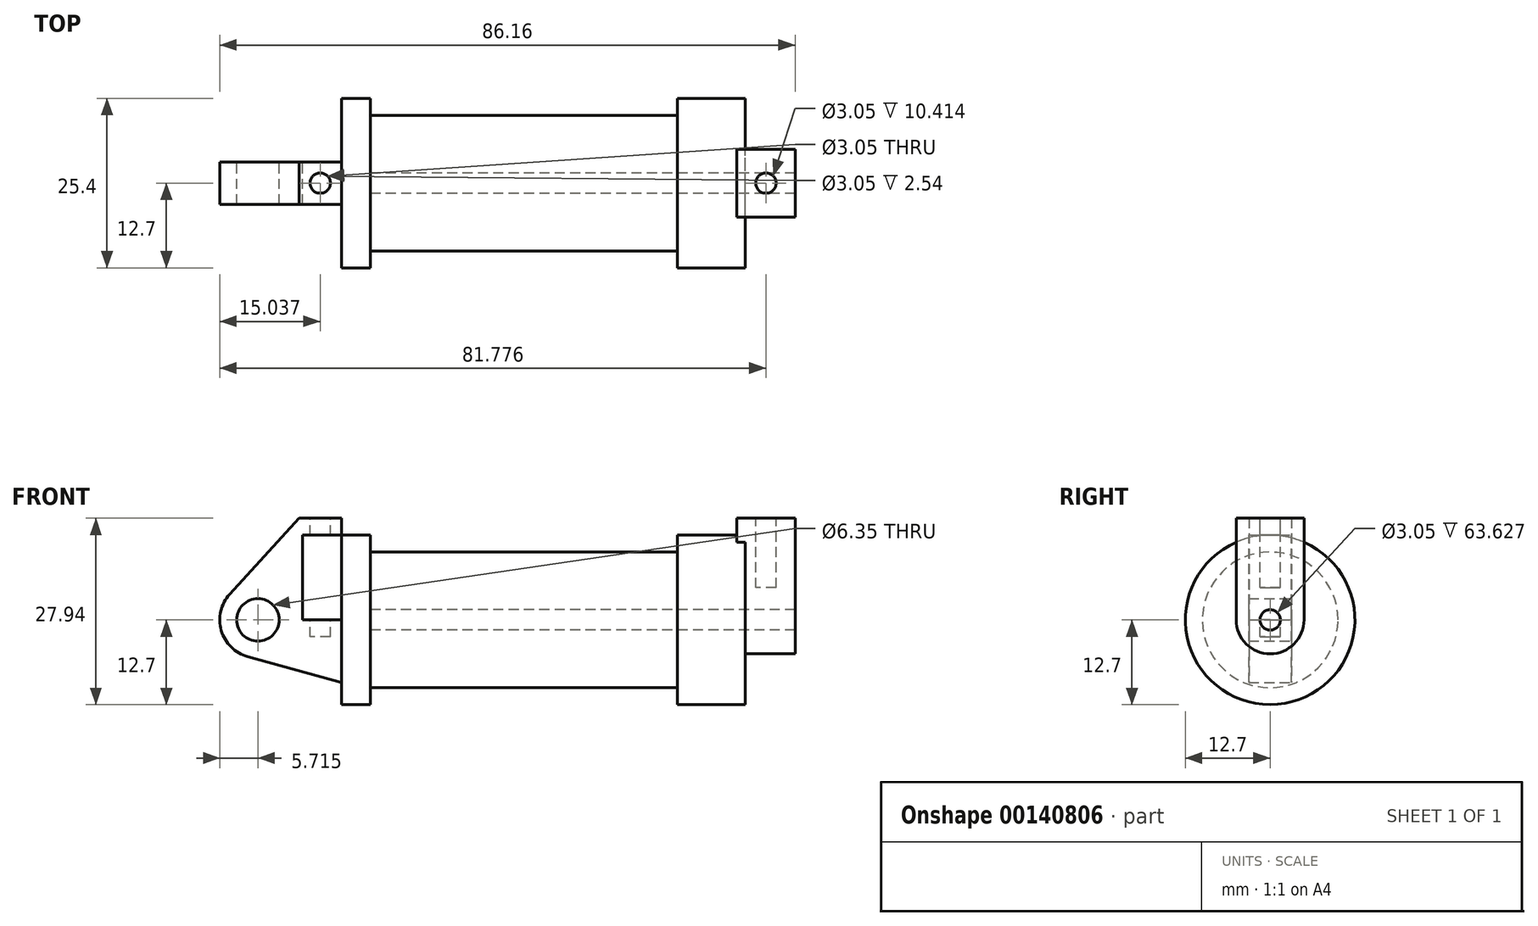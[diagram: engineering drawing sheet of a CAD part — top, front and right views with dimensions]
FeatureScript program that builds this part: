
annotation { "Feature Type Name" : "Feature", "Feature Type Description" : "" }
export const myFeature = defineFeature(function(context is Context, id is Id, definition is map)
    precondition{}
    {
        {
            var Q0;
            Q0=qCreatedBy(makeId("Front.planeOp"),FACE);
            var sketch = newSketch(context, id + "F0", { "sketchPlane" : qUnion([Q0])});
            skLineSegment(sketch, "E0", {"start": v(0, 0) * mm, "end": v(0, 12.7) * mm});
            skLineSegment(sketch, "E1", {"start": v(0, 12.7) * mm, "end": v(10.16, 12.7) * mm});
            skLineSegment(sketch, "E2", {"start": v(10.16, 12.7) * mm, "end": v(10.16, 10.16) * mm});
            skLineSegment(sketch, "E3", {"start": v(10.16, 10.16) * mm, "end": v(56.13, 10.16) * mm});
            skLineSegment(sketch, "E4", {"start": v(56.13, 10.16) * mm, "end": v(56.13, 12.7) * mm});
            skLineSegment(sketch, "E5", {"start": v(56.13, 12.7) * mm, "end": v(66.3, 12.7) * mm});
            skLineSegment(sketch, "E6", {"start": v(66.3, 12.7) * mm, "end": v(66.3, 0) * mm});
            skLineSegment(sketch, "E7", {"start": v(66.3, 0) * mm, "end": v(0, 0) * mm});
            skLineSegment(sketch, "E8", {"start": v(5.84, 15.24) * mm, "end": v(-0.5, 15.24) * mm});
            skLineSegment(sketch, "E9", {"start": v(-0.5, 15.24) * mm, "end": v(-10.88, 3.85) * mm});
            skLineSegment(sketch, "E10", {"start": v(0, 0) * mm, "end": v(-6.65, 0) * mm});
            skCircle(sketch, "E11", {"center": v(-6.65, 0) * mm, "radius": 5.72 * mm});
            skCircle(sketch, "E12", {"center": v(-6.65, 0) * mm, "radius": 3.18 * mm});
            skLineSegment(sketch, "E13", {"start": v(5.84, 15.24) * mm, "end": v(5.84, -9.4) * mm});
            skLineSegment(sketch, "E14", {"start": v(5.84, -9.4) * mm, "end": v(-8.18, -5.5) * mm});
            skSolve(sketch);
        }
        {
            var Q0;
            {var subQ3=sQuery(id+"F0.wireOp",EDGE,"E0");Q0=makeQuery(id+"F0.imprint","IMPRINT",FACE,{"disambiguationData":[TD([[makeQuery(id+"F0.imprint","IMPRINT",EDGE,{"derivedFrom":subQ3}),1.0]])]});}
            var Q1;
            {var subQ0=sQuery(id+"F0.wireOp",EDGE,"E14");Q1=makeQuery(id+"F0.imprint","IMPRINT",FACE,{"disambiguationData":[TD([[makeQuery(id+"F0.imprint","IMPRINT",EDGE,{"derivedFrom":subQ0}),-1.0]])]});}
            var Q2;
            {var subQ4=sQuery(id+"F0.wireOp",EDGE,"E12");Q2=makeQuery(id+"F0.imprint","IMPRINT",FACE,{"disambiguationData":[TD([[makeQuery(id+"F0.imprint","IMPRINT",EDGE,{"derivedFrom":subQ4}),-1.0]])]});}
            extrude(context, id + "F1", {"entities" : qUnion([Q0, Q1, Q2]), "endBound" : BoundingType.SYMMETRIC, "depth" : 6.35 * mm});
        }
        {
            var Q0;
            {var subQ0=sQuery(id+"F0.wireOp",EDGE,"E2");Q0=makeQuery(id+"F0.imprint","IMPRINT",FACE,{"disambiguationData":[TD([[makeQuery(id+"F0.imprint","IMPRINT",EDGE,{"derivedFrom":subQ0}),-1.0]])]});}
            var Q1;
            Q1=sQuery(id+"F0.wireOp",EDGE,"E7");
            revolve(context, id + "F2", {"entities" : qUnion([Q0]), "axis" : qUnion([Q1]), "revolveType" : RevolveType.FULL});
        }
        {
            var Q0;
            Q0=makeQuery(id+"F2.opRevolve","SWEPT_FACE",FACE,{"disambiguationData":[OSD([sQuery(id+"F0.wireOp",EDGE,"E6")])]});
            var sketch = newSketch(context, id + "F3", { "sketchPlane" : qUnion([Q0])});
            skCircle(sketch, "E15", {"center": v(0, 0) * mm, "radius": 1.52 * mm});
            skCircle(sketch, "E16", {"center": v(0, 0) * mm, "radius": 5.08 * mm});
            skLineSegment(sketch, "E17", {"start": v(-5.08, 0) * mm, "end": v(-5.08, 15.24) * mm});
            skLineSegment(sketch, "E18", {"start": v(5.08, 0) * mm, "end": v(5.08, 15.24) * mm});
            skLineSegment(sketch, "E19", {"start": v(5.08, 15.24) * mm, "end": v(-5.08, 15.24) * mm});
            skSolve(sketch);
        }
        {
            var Q0;
            Q0 = qSketchRegion(id + "F3", true);
            extrude(context, id + "F4", {"entities" : qUnion([Q0]), "operationType" : NewBodyOperationType.ADD, "oppositeDirection" : true, "depth" : 1.27 * mm});
        }
        {
            var Q0;
            Q0 = qSketchRegion(id + "F3", true);
            extrude(context, id + "F5", {"entities" : qUnion([Q0]), "operationType" : NewBodyOperationType.ADD, "depth" : 7.5 * mm});
        }
        {
            var Q0;
            Q0=makeQuery(id+"F3.imprint","IMPRINT",FACE,{"disambiguationData":[TD([[makeQuery(id+"F3.imprint","IMPRINT",EDGE,{"derivedFrom":sQuery(id+"F3.wireOp",EDGE,"E15")}),1.0]])]});
            var Q1;
            Q1=sQuery(id+"F3.wireOp",EDGE,"E15");
            var Q2;
            Q2=makeQuery(id+"F2.opRevolve","SWEPT_FACE",FACE,{"disambiguationData":[OSD([sQuery(id+"F0.wireOp",EDGE,"E2")])]});
            extrude(context, id + "F6", {"entities" : qUnion([Q0]), "operationType" : NewBodyOperationType.REMOVE, "surfaceEntities" : qUnion([Q1]), "endBound" : BoundingType.UP_TO_SURFACE, "oppositeDirection" : true, "endBoundEntityFace" : qUnion([Q2]), "depth" : 25.4 * mm});
        }
        {
            var Q0;
            {var subQ0=sQuery(id+"F3.wireOp",EDGE,"E19");Q0=makeQuery(id+"F5.boolean.opBoolean","MERGE",FACE,{"derivedFrom":[makeQuery(id+"F4.opExtrude","SWEPT_FACE",FACE,{"disambiguationData":[OSD([subQ0])]}),makeQuery(id+"F5.opExtrude","SWEPT_FACE",FACE,{"disambiguationData":[OSD([subQ0])]})]});}
            var sketch = newSketch(context, id + "F7", { "sketchPlane" : qUnion([Q0])});
            skCircle(sketch, "E20", {"center": v(69.4, 0) * mm, "radius": 1.52 * mm});
            skPoint(sketch, "E20.centerSnap0", {"position": v(69.4, 5.08) * mm});
            skPoint(sketch, "E20.centerSnap1", {"position": v(73.79, 0) * mm});
            skSolve(sketch);
        }
        {
            var Q0;
            Q0=makeQuery(id+"F1.opExtrude","SWEPT_FACE",FACE,{"disambiguationData":[OSD([sQuery(id+"F0.wireOp",EDGE,"E8")])]});
            var sketch = newSketch(context, id + "F8", { "sketchPlane" : qUnion([Q0])});
            skCircle(sketch, "E21", {"center": v(2.67, 0) * mm, "radius": 1.52 * mm});
            skPoint(sketch, "E21.centerSnap0", {"position": v(5.84, 0) * mm});
            skPoint(sketch, "E21.centerSnap1", {"position": v(2.67, 3.18) * mm});
            skSolve(sketch);
        }
        {
            var Q0;
            Q0=makeQuery(id+"F7.imprint","IMPRINT",FACE,{"disambiguationData":[TD([[makeQuery(id+"F7.imprint","IMPRINT",EDGE,{"derivedFrom":sQuery(id+"F7.wireOp",EDGE,"E20")}),1.0]])]});
            var Q1;
            Q1=sQuery(id+"F7.wireOp",EDGE,"E20");
            extrude(context, id + "F9", {"entities" : qUnion([Q0]), "operationType" : NewBodyOperationType.REMOVE, "surfaceEntities" : qUnion([Q1]), "oppositeDirection" : true, "depth" : 10.4 * mm});
        }
        {
            var Q0;
            Q0=makeQuery(id+"F8.imprint","IMPRINT",FACE,{"disambiguationData":[TD([[makeQuery(id+"F8.imprint","IMPRINT",EDGE,{"derivedFrom":sQuery(id+"F8.wireOp",EDGE,"E21")}),1.0]])]});
            extrude(context, id + "F10", {"entities" : qUnion([Q0]), "operationType" : NewBodyOperationType.REMOVE, "oppositeDirection" : true, "depth" : 17.78 * mm});
        }
    });
